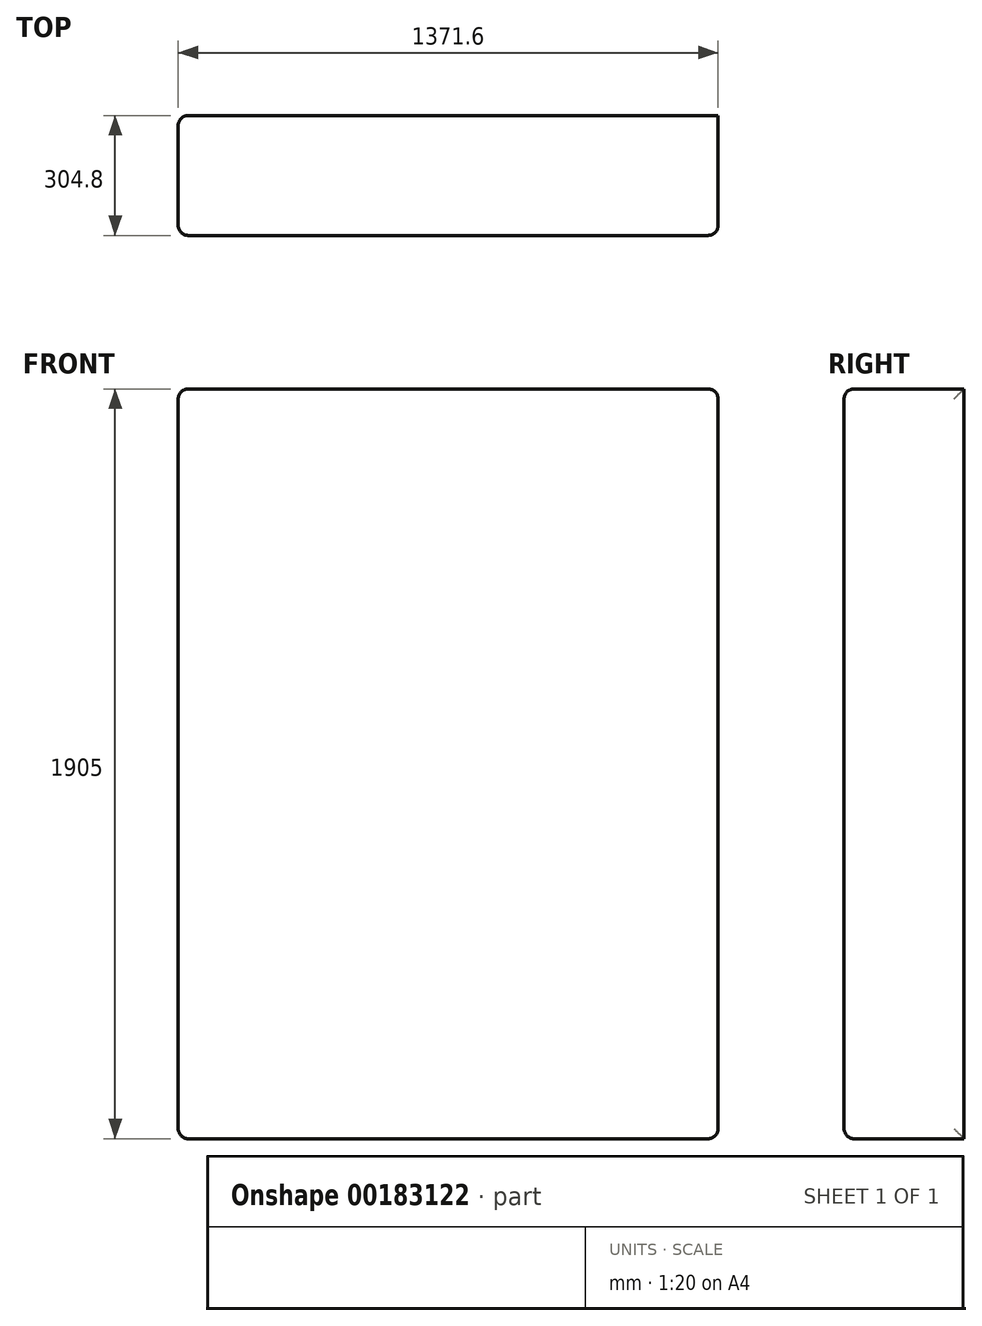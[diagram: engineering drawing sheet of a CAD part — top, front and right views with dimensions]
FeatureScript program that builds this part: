
annotation { "Feature Type Name" : "Feature", "Feature Type Description" : "" }
export const myFeature = defineFeature(function(context is Context, id is Id, definition is map)
    precondition{}
    {
        {
            var Q0;
            Q0=qCreatedBy(makeId("Front.planeOp"),FACE);
            var sketch = newSketch(context, id + "F0", { "sketchPlane" : qUnion([Q0])});
            skLineSegment(sketch, "E0.bottom", {"start": v(0, 0) * mm, "end": v(1371.6, 0) * mm});
            skLineSegment(sketch, "E0.top", {"start": v(0, 1905) * mm, "end": v(1371.6, 1905) * mm});
            skLineSegment(sketch, "E0.left", {"start": v(0, 0) * mm, "end": v(0, 1905) * mm});
            skLineSegment(sketch, "E0.right", {"start": v(1371.6, 0) * mm, "end": v(1371.6, 1905) * mm});
            skSolve(sketch);
        }
        {
            var Q0;
            Q0 = qSketchRegion(id + "F0", true);
            extrude(context, id + "F1", {"entities" : qUnion([Q0]), "depth" : 304.8 * mm});
        }
        {
            var Q0;
            Q0=makeQuery(id+"F1.opExtrude","CAP_FACE",FACE,{"disambiguationData":[OSD([sQuery(id+"F0.wireOp",EDGE,"E0.bottom"),sQuery(id+"F0.wireOp",EDGE,"E0.top"),sQuery(id+"F0.wireOp",EDGE,"E0.left"),sQuery(id+"F0.wireOp",EDGE,"E0.right")])],"isStart":false});
            var Q1;
            Q1=makeQuery(id+"F1.opExtrude","SWEPT_EDGE",EDGE,{"disambiguationData":[OSD([sQuery(id+"F0.wireOp",EDGE,"E0.bottom"),sQuery(id+"F0.wireOp",EDGE,"E0.right")])]});
            var Q2;
            Q2=makeQuery(id+"F1.opExtrude","SWEPT_EDGE",EDGE,{"disambiguationData":[OSD([sQuery(id+"F0.wireOp",EDGE,"E0.bottom"),sQuery(id+"F0.wireOp",EDGE,"E0.left")])]});
            var Q3;
            Q3=makeQuery(id+"F1.opExtrude","SWEPT_FACE",FACE,{"disambiguationData":[OSD([sQuery(id+"F0.wireOp",EDGE,"E0.left")])]});
            var Q4;
            Q4=makeQuery(id+"F1.opExtrude","SWEPT_EDGE",EDGE,{"disambiguationData":[OSD([sQuery(id+"F0.wireOp",EDGE,"E0.top"),sQuery(id+"F0.wireOp",EDGE,"E0.right")])]});
            fillet(context, id + "F2", {"entities" : qUnion([Q0, Q1, Q2, Q3, Q4]), "radius" : 25.4 * mm, "tangentPropagation" : true, "allowEdgeOverflow" : false});
        }
    });
